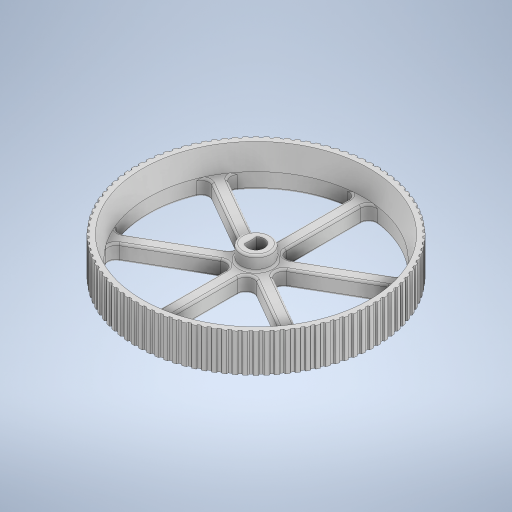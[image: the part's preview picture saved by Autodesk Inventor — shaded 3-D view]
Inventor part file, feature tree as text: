
AUTODESK INVENTOR PART (.ipt)
format: ipt  version: 2024.2 (Build 282272000, 272)  size: 1,033,728 bytes
history: native  units: mm
features: sketch x3, extrude x3, fillet x2, revolve x1
ambient origin geometry x8: Origin, YZ Plane, XZ Plane, XY Plane, X Axis, Y Axis, Z Axis, Center Point
bodies: Solid1 (feature_tree)
feature tree (9):
  revolve  "Revolution1"  [1 undecoded]
  sketch  "Sketch3"  dims[d3=30.0mm d4=360.0deg]
  extrude  "Extrusion1"  TaperAngle=360.0deg  [1 undecoded]
  extrude  "Extrusion2"  Depth=10.0mm
  extrude  "Extrusion3"  Depth=0.5mm
  fillet  "Fillet1"  Radius=3.0mm
  fillet  "Fillet2"  Radius=1.5mm
  sketch  "Sketch2"  dims[d0=3.0mm d2=4.0mm]
  sketch  "Sketch4"  dims[d5=4.15mm d7=10.0mm d8=7.5mm d9=3.0mm d10=1.5mm d11=60.0mm d13=360.0deg d15=4.0mm d16=0.0mm d17=7.5mm d18=0.0mm d19=120.0deg d20=120.0deg d21=1.6mm d22=1.0mm d23=0.5mm d24=1000.0mm d26=360.0deg d28=0.0mm d29=0.0mm d30=2.0mm d31=0.5mm d37=1.5mm d38=9.5mm d39=3.5mm d32=0.0mm d33=0.0mm d34=0.0mm d35=0.0mm]
note: 2 required parameter values undecoded (feature->parameter linkage not recoverable at this tier; creation-order binding heuristic only, values carry confidence <= 0.55)